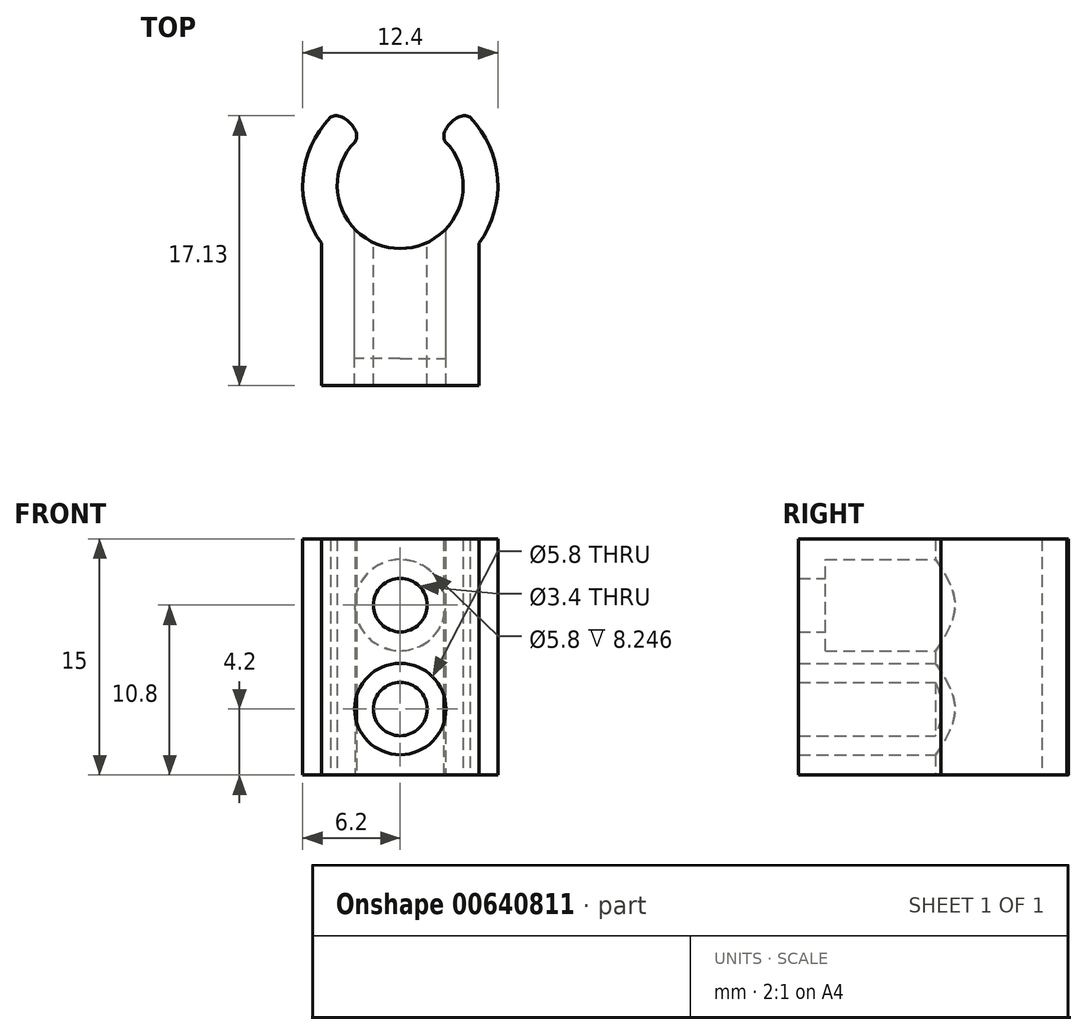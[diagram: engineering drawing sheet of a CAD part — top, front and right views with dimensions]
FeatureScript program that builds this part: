
annotation { "Feature Type Name" : "Feature", "Feature Type Description" : "" }
export const myFeature = defineFeature(function(context is Context, id is Id, definition is map)
    precondition{}
    {
        {
            var Q0;
            Q0=qCreatedBy(makeId("Top.planeOp"),FACE);
            var sketch = newSketch(context, id + "F0", { "sketchPlane" : qUnion([Q0])});
            skCircle(sketch, "E0", {"center": v(0, 0) * mm, "radius": 4 * mm});
            skCircle(sketch, "E1", {"center": v(0, 0) * mm, "radius": 6.2 * mm});
            skLineSegment(sketch, "E2", {"start": v(-7.8, -12.7) * mm, "end": v(14.21, -12.7) * mm, "construction": true});
            skLineSegment(sketch, "E3", {"start": v(-5, -3.67) * mm, "end": v(-5, -12.7) * mm});
            skLineSegment(sketch, "E4", {"start": v(-5, -12.7) * mm, "end": v(0, -12.7) * mm});
            skLineSegment(sketch, "E5.MirrorCS", {"start": v(5, -3.67) * mm, "end": v(5, -12.7) * mm});
            skLineSegment(sketch, "E6", {"start": v(0, -12.7) * mm, "end": v(5, -12.7) * mm});
            skLineSegment(sketch, "E7", {"start": v(-3, 0) * mm, "end": v(-3, 9.22) * mm, "construction": true});
            skLineSegment(sketch, "E8", {"start": v(-4, 0) * mm, "end": v(-4, 10.25) * mm, "construction": true});
            skLineSegment(sketch, "E9.MirrorCS", {"start": v(3, 0) * mm, "end": v(3, 9.22) * mm, "construction": true});
            skLineSegment(sketch, "E10.MirrorCS", {"start": v(4, 0) * mm, "end": v(4, 10.25) * mm, "construction": true});
            skFitSpline(sketch, "E11", {"points": [v(-3, 2.65) * mm, v(-4.62, 4.14) * mm], "startDerivative": vector(2.63, 2.23) * mm, "endDerivative": vector(-1.8, -2.95) * mm});
            skFitSpline(sketch, "E12.MirrorCS", {"points": [v(3, 2.65) * mm, v(4.62, 4.14) * mm], "startDerivative": vector(-2.63, 2.23) * mm, "endDerivative": vector(1.8, -2.95) * mm});
            skSolve(sketch);
        }
        {
            var Q0;
            {var subQ0=sQuery(id+"F0.wireOp",EDGE,"E12.MirrorCS");var subQ6=sQuery(id+"F0.wireOp",EDGE,"E0");var subQ9=makeQuery(id+"F0.imprint","INTERSECT",VERTEX,{"disambiguationData":[OD(0.0)],"derivedFrom":[subQ6,subQ0]});Q0=makeQuery(id+"F0.imprint","IMPRINT",FACE,{"disambiguationData":[TD([[makeQuery(id+"F0.imprint","IMPRINT",EDGE,{"disambiguationData":[TD([[subQ9,-1.0]])],"derivedFrom":subQ6}),-1.0]])]});}
            var Q1;
            {var subQ1=sQuery(id+"F0.wireOp",EDGE,"E3");Q1=makeQuery(id+"F0.imprint","IMPRINT",FACE,{"disambiguationData":[TD([[makeQuery(id+"F0.imprint","IMPRINT",EDGE,{"derivedFrom":subQ1}),1.0]])]});}
            extrude(context, id + "F1", {"entities" : qUnion([Q0, Q1]), "depth" : 15 * mm, "offsetDistance" : 25 * mm});
        }
        {
            var Q0;
            Q0=qCreatedBy(makeId("Front.planeOp"),FACE);
            var sketch = newSketch(context, id + "F2", { "sketchPlane" : qUnion([Q0])});
            skCircle(sketch, "E13", {"center": v(0, 10.8) * mm, "radius": 2.9 * mm});
            skCircle(sketch, "E14", {"center": v(0, 10.8) * mm, "radius": 1.7 * mm});
            skLineSegment(sketch, "E15", {"start": v(8.45, 7.5) * mm, "end": v(2.33, 7.5) * mm, "construction": true});
            skCircle(sketch, "E16.MirrorC", {"center": v(0, 4.2) * mm, "radius": 2.9 * mm});
            skCircle(sketch, "E17.MirrorC", {"center": v(0, 4.2) * mm, "radius": 1.7 * mm});
            skSolve(sketch);
        }
        {
            var Q0;
            Q0=makeQuery(id+"F2.imprint","IMPRINT",FACE,{"disambiguationData":[TD([[makeQuery(id+"F2.imprint","IMPRINT",EDGE,{"derivedFrom":sQuery(id+"F2.wireOp",EDGE,"E14")}),1.0]])]});
            var Q1;
            Q1=makeQuery(id+"F2.imprint","IMPRINT",FACE,{"disambiguationData":[TD([[makeQuery(id+"F2.imprint","IMPRINT",EDGE,{"derivedFrom":sQuery(id+"F2.wireOp",EDGE,"E17.MirrorC")}),-1.0]])]});
            extrude(context, id + "F3", {"entities" : qUnion([Q0, Q1]), "operationType" : NewBodyOperationType.REMOVE, "oppositeDirection" : true, "depth" : -25 * mm, "offsetDistance" : 25 * mm});
        }
        {
            var Q0;
            Q0=makeQuery(id+"F2.imprint","IMPRINT",FACE,{"disambiguationData":[TD([[makeQuery(id+"F2.imprint","IMPRINT",EDGE,{"derivedFrom":sQuery(id+"F2.wireOp",EDGE,"E13")}),1.0]])]});
            var Q1;
            Q1=makeQuery(id+"F2.imprint","IMPRINT",FACE,{"disambiguationData":[TD([[makeQuery(id+"F2.imprint","IMPRINT",EDGE,{"derivedFrom":sQuery(id+"F2.wireOp",EDGE,"867ee87d-e075-4b43-8604-5dc8acbfab4a0.MirrorC")}),1.0]])]});
            var Q2;
            Q2=makeQuery(id+"F2.imprint","IMPRINT",FACE,{"disambiguationData":[TD([[makeQuery(id+"F2.imprint","IMPRINT",EDGE,{"derivedFrom":sQuery(id+"F2.wireOp",EDGE,"E16.MirrorC")}),-1.0]])]});
            extrude(context, id + "F4", {"entities" : qUnion([Q0, Q1, Q2]), "operationType" : NewBodyOperationType.REMOVE, "depth" : 11 * mm, "offsetDistance" : 25 * mm});
        }
    });
